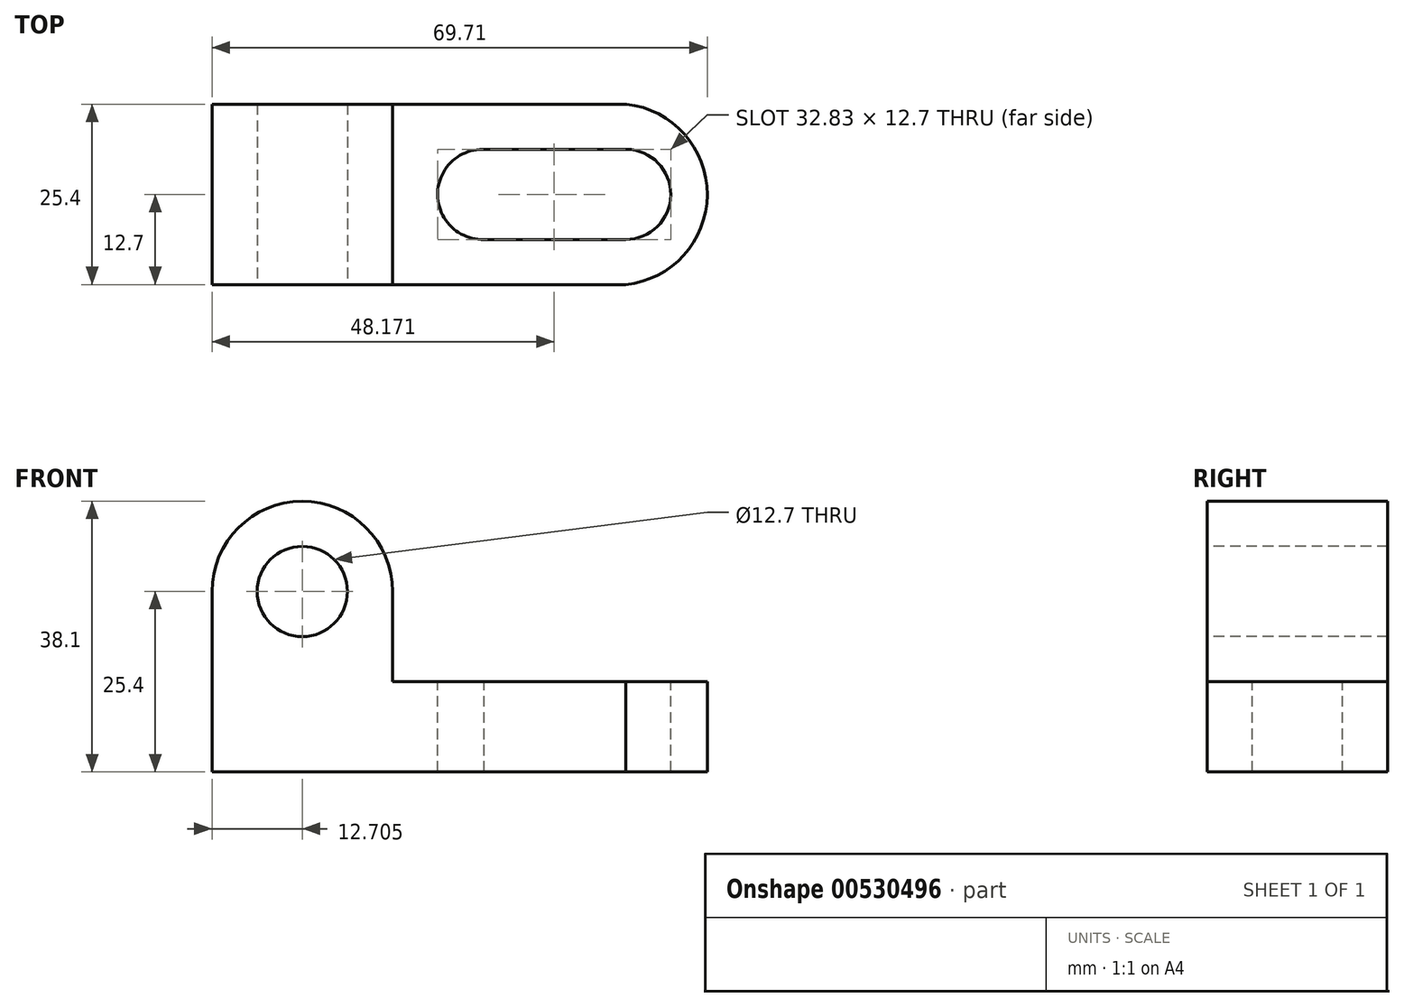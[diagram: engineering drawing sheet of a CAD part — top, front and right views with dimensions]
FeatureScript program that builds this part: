
annotation { "Feature Type Name" : "Feature", "Feature Type Description" : "" }
export const myFeature = defineFeature(function(context is Context, id is Id, definition is map)
    precondition{}
    {
        {
            var Q0;
            Q0=qCreatedBy(makeId("Front.planeOp"),FACE);
            var sketch = newSketch(context, id + "F0", { "sketchPlane" : qUnion([Q0])});
            skLineSegment(sketch, "E0", {"start": v(-71.86, 38.1) * mm, "end": v(-71.86, 0) * mm});
            skLineSegment(sketch, "E1", {"start": v(-71.86, 0) * mm, "end": v(-2, 0) * mm});
            skLineSegment(sketch, "E2", {"start": v(-2, 0) * mm, "end": v(-2, 12.7) * mm});
            skLineSegment(sketch, "E3", {"start": v(-2, 12.7) * mm, "end": v(-46.46, 12.7) * mm});
            skLineSegment(sketch, "E4", {"start": v(-46.46, 12.7) * mm, "end": v(-46.46, 38.1) * mm});
            skLineSegment(sketch, "E5", {"start": v(-46.46, 38.1) * mm, "end": v(-71.86, 38.1) * mm});
            skLineSegment(sketch, "E6", {"start": v(-2, 12.7) * mm, "end": v(-2, 0) * mm});
            skSolve(sketch);
        }
        {
            var Q0;
            Q0 = qSketchRegion(id + "F0", true);
            extrude(context, id + "F1", {"entities" : qUnion([Q0]), "depth" : 25.4 * mm, "offsetDistance" : 25.4 * mm});
        }
        {
            var Q0;
            Q0=makeQuery(id+"F1.opExtrude","CAP_FACE",FACE,{"disambiguationData":[OSD([sQuery(id+"F0.wireOp",EDGE,"E0"),sQuery(id+"F0.wireOp",EDGE,"E1"),sQuery(id+"F0.wireOp",EDGE,"E3"),sQuery(id+"F0.wireOp",EDGE,"E4"),sQuery(id+"F0.wireOp",EDGE,"E5"),sQuery(id+"F0.wireOp",EDGE,"E6")])],"isStart":false});
            var sketch = newSketch(context, id + "F2", { "sketchPlane" : qUnion([Q0])});
            skCircle(sketch, "E7", {"center": v(-59.16, 25.4) * mm, "radius": 6.35 * mm});
            skSolve(sketch);
        }
        {
            var Q0;
            Q0=makeQuery(id+"F2.imprint","IMPRINT",FACE,{"disambiguationData":[TD([[makeQuery(id+"F2.imprint","IMPRINT",EDGE,{"derivedFrom":sQuery(id+"F2.wireOp",EDGE,"E7")}),1.0]])]});
            extrude(context, id + "F3", {"entities" : qUnion([Q0]), "operationType" : NewBodyOperationType.REMOVE, "endBound" : BoundingType.THROUGH_ALL, "oppositeDirection" : true, "depth" : 25.4 * mm, "offsetDistance" : 25.4 * mm});
        }
        {
            var Q0;
            Q0=makeQuery(id+"F1.opExtrude","CAP_FACE",FACE,{"disambiguationData":[OSD([sQuery(id+"F0.wireOp",EDGE,"E0"),sQuery(id+"F0.wireOp",EDGE,"E1"),sQuery(id+"F0.wireOp",EDGE,"E3"),sQuery(id+"F0.wireOp",EDGE,"E4"),sQuery(id+"F0.wireOp",EDGE,"E5"),sQuery(id+"F0.wireOp",EDGE,"E6")])],"isStart":false});
            var sketch = newSketch(context, id + "F4", { "sketchPlane" : qUnion([Q0])});
            skArc(sketch, "E8", {"start": v(-46.46, 25.4) * mm, "mid": v(-59.16, 38.1) * mm, "end": v(-71.86, 25.4) * mm});
            skSolve(sketch);
        }
        {
            var Q0;
            Q0 = qSketchRegion(id + "F4", true);
            var Q1;
            {var subQ0=sQuery(id+"F4.wireOp",EDGE,"D0o1SrTt-Ggtp-pL1r-cdHS-uXgKJroGG82g");var subQ1=makeQuery(id+"F1.opExtrude","CAP_EDGE",EDGE,{"disambiguationData":[OSD([sQuery(id+"F0.wireOp",EDGE,"E0")])],"isStart":false});var subQ2=makeQuery(id+"F4.imprint","INTERSECT",VERTEX,{"derivedFrom":[subQ1,subQ0]});Q1=makeQuery(id+"F4.imprint","IMPRINT",FACE,{"disambiguationData":[TD([[makeQuery(id+"F4.imprint","IMPRINT",EDGE,{"disambiguationData":[TD([[subQ2,1.0]])],"derivedFrom":subQ0}),-1.0]])]});}
            var Q2;
            {var subQ0=sQuery(id+"F4.wireOp",EDGE,"D0o1SrTt-Ggtp-pL1r-cdHS-uXgKJroGG82g");var subQ1=makeQuery(id+"F1.opExtrude","CAP_EDGE",EDGE,{"disambiguationData":[OSD([sQuery(id+"F0.wireOp",EDGE,"E4")])],"isStart":false});var subQ2=makeQuery(id+"F4.imprint","INTERSECT",VERTEX,{"derivedFrom":[subQ1,subQ0]});Q2=makeQuery(id+"F4.imprint","IMPRINT",FACE,{"disambiguationData":[TD([[makeQuery(id+"F4.imprint","IMPRINT",EDGE,{"disambiguationData":[TD([[subQ2,-1.0]])],"derivedFrom":subQ0}),-1.0]])]});}
            var Q3;
            {var subQ0=sQuery(id+"F4.wireOp",EDGE,"E8");var subQ1=makeQuery(id+"F1.opExtrude","CAP_EDGE",EDGE,{"disambiguationData":[OSD([sQuery(id+"F0.wireOp",EDGE,"E0")])],"isStart":false});var subQ2=makeQuery(id+"F4.imprint","INTERSECT",VERTEX,{"derivedFrom":[subQ1,subQ0]});Q3=makeQuery(id+"F4.imprint","IMPRINT",FACE,{"disambiguationData":[TD([[makeQuery(id+"F4.imprint","IMPRINT",EDGE,{"disambiguationData":[TD([[subQ2,1.0]])],"derivedFrom":subQ0}),-1.0]])]});}
            var Q4;
            {var subQ0=sQuery(id+"F4.wireOp",EDGE,"E8");var subQ1=makeQuery(id+"F1.opExtrude","CAP_EDGE",EDGE,{"disambiguationData":[OSD([sQuery(id+"F0.wireOp",EDGE,"E4")])],"isStart":false});var subQ2=makeQuery(id+"F4.imprint","INTERSECT",VERTEX,{"derivedFrom":[subQ1,subQ0]});Q4=makeQuery(id+"F4.imprint","IMPRINT",FACE,{"disambiguationData":[TD([[makeQuery(id+"F4.imprint","IMPRINT",EDGE,{"disambiguationData":[TD([[subQ2,-1.0]])],"derivedFrom":subQ0}),-1.0]])]});}
            extrude(context, id + "F5", {"entities" : qUnion([Q0, Q1, Q2, Q3, Q4]), "operationType" : NewBodyOperationType.REMOVE, "endBound" : BoundingType.THROUGH_ALL, "oppositeDirection" : true, "depth" : 25.4 * mm, "offsetDistance" : 25.4 * mm});
        }
        {
            var Q0;
            Q0=makeQuery(id+"F1.opExtrude","SWEPT_FACE",FACE,{"disambiguationData":[OSD([sQuery(id+"F0.wireOp",EDGE,"E3")])]});
            var sketch = newSketch(context, id + "F6", { "sketchPlane" : qUnion([Q0])});
            skCircle(sketch, "E9", {"center": v(-33.76, -12.7) * mm, "radius": 6.35 * mm});
            skPoint(sketch, "E9.centerSnap0", {"position": v(-46.46, -12.7) * mm});
            skCircle(sketch, "E10", {"center": v(-13.62, -12.7) * mm, "radius": 6.35 * mm});
            skLineSegment(sketch, "E11", {"start": v(-33.56, -19.05) * mm, "end": v(-13.62, -19.05) * mm});
            skLineSegment(sketch, "E12", {"start": v(-13.5, -6.35) * mm, "end": v(-33.75, -6.35) * mm});
            skArc(sketch, "E13", {"start": v(-13.62, -25.4) * mm, "mid": v(-2.15, -12.75) * mm, "end": v(-13.5, 0) * mm});
            skSolve(sketch);
        }
        {
            var Q0;
            {var subQ0=sQuery(id+"F6.wireOp",EDGE,"E12");var subQ1=sQuery(id+"F6.wireOp",EDGE,"E10");var subQ2=makeQuery(id+"F6.imprint","INTERSECT",VERTEX,{"disambiguationData":[OD(0.0)],"derivedFrom":[subQ1,subQ0]});Q0=makeQuery(id+"F6.imprint","IMPRINT",FACE,{"disambiguationData":[TD([[makeQuery(id+"F6.imprint","IMPRINT",EDGE,{"disambiguationData":[TD([[subQ2,-1.0]])],"derivedFrom":subQ1}),1.0]])]});}
            var Q1;
            {var subQ0=sQuery(id+"F6.wireOp",EDGE,"E10");var subQ1=makeQuery(id+"F6.imprint","INTERSECT",VERTEX,{"derivedFrom":[subQ0,sQuery(id+"F6.wireOp",EDGE,"E11")]});Q1=makeQuery(id+"F6.imprint","IMPRINT",FACE,{"disambiguationData":[TD([[makeQuery(id+"F6.imprint","IMPRINT",EDGE,{"disambiguationData":[TD([[subQ1,1.0]])],"derivedFrom":subQ0}),1.0]])]});}
            var Q2;
            {var subQ0=sQuery(id+"F6.wireOp",EDGE,"E11");Q2=makeQuery(id+"F6.imprint","IMPRINT",FACE,{"disambiguationData":[TD([[makeQuery(id+"F6.imprint","IMPRINT",EDGE,{"derivedFrom":subQ0}),1.0]])]});}
            var Q3;
            {var subQ0=sQuery(id+"F6.wireOp",EDGE,"E9");var subQ1=makeQuery(id+"F6.imprint","INTERSECT",VERTEX,{"derivedFrom":[subQ0,sQuery(id+"F6.wireOp",EDGE,"E11")]});Q3=makeQuery(id+"F6.imprint","IMPRINT",FACE,{"disambiguationData":[TD([[makeQuery(id+"F6.imprint","IMPRINT",EDGE,{"disambiguationData":[TD([[subQ1,1.0]])],"derivedFrom":subQ0}),1.0]])]});}
            var Q4;
            {var subQ0=sQuery(id+"F6.wireOp",EDGE,"E13");Q4=makeQuery(id+"F6.imprint","IMPRINT",FACE,{"disambiguationData":[TD([[makeQuery(id+"F6.imprint","IMPRINT",EDGE,{"derivedFrom":subQ0}),-1.0]])]});}
            extrude(context, id + "F7", {"entities" : qUnion([Q0, Q1, Q2, Q3, Q4]), "operationType" : NewBodyOperationType.REMOVE, "endBound" : BoundingType.THROUGH_ALL, "oppositeDirection" : true, "depth" : 25.4 * mm, "offsetDistance" : 25.4 * mm});
        }
    });
